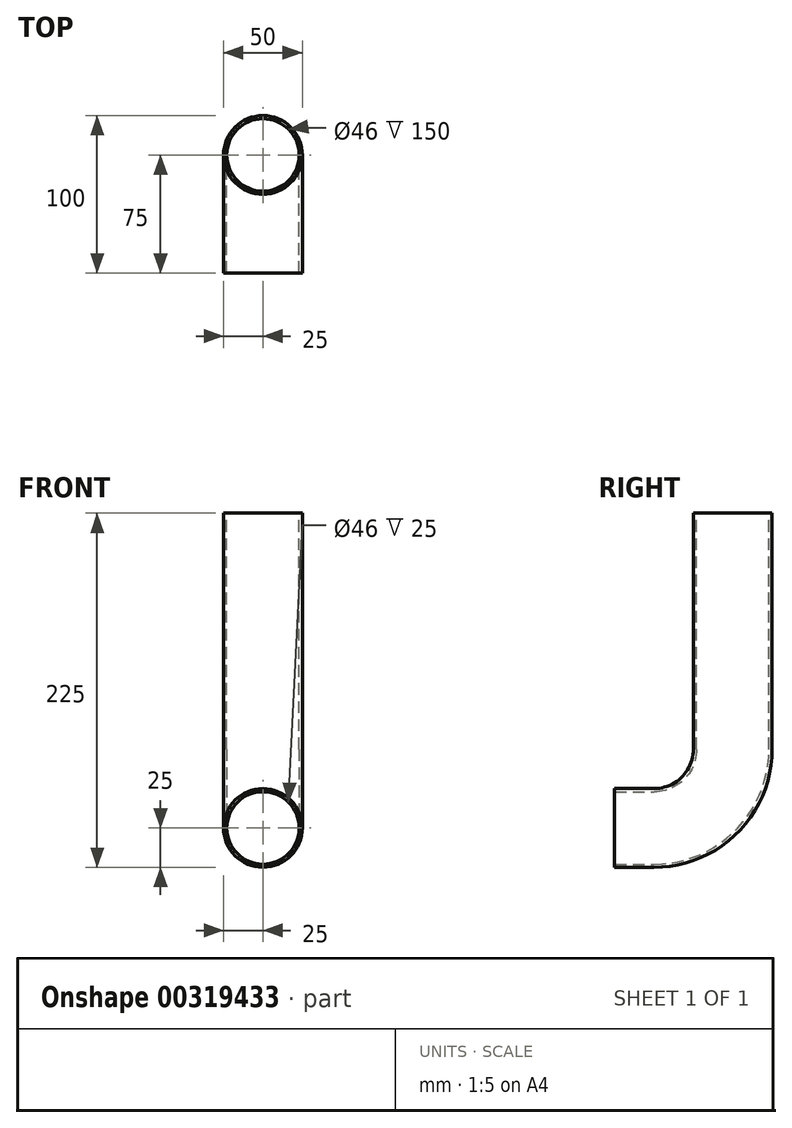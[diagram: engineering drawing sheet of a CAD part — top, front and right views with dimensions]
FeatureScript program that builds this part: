
annotation { "Feature Type Name" : "Feature", "Feature Type Description" : "" }
export const myFeature = defineFeature(function(context is Context, id is Id, definition is map)
    precondition{}
    {
        {
            var Q0;
            Q0=qCreatedBy(makeId("Front.planeOp"),FACE);
            var sketch = newSketch(context, id + "F0", { "sketchPlane" : qUnion([Q0])});
            skCircle(sketch, "E0", {"center": v(0, 0) * mm, "radius": 25 * mm});
            skCircle(sketch, "E1", {"center": v(0, 0) * mm, "radius": 23 * mm});
            skSolve(sketch);
        }
        {
            var Q0;
            Q0=qCreatedBy(makeId("Right.planeOp"),FACE);
            var sketch = newSketch(context, id + "F1", { "sketchPlane" : qUnion([Q0])});
            skLineSegment(sketch, "E2", {"start": v(0, 0) * mm, "end": v(25, 0) * mm});
            skLineSegment(sketch, "E3", {"start": v(75, 50) * mm, "end": v(75, 200) * mm});
            skArc(sketch, "E4", {"start": v(75, 50) * mm, "mid": v(60.36, 14.64) * mm, "end": v(25, 0) * mm});
            skSolve(sketch);
        }
        {
            var Q0;
            Q0 = qSketchRegion(id + "F0", true);
            var Q1;
            Q1 = qBodyType(qCreatedBy(id + "F1" ,EDGE), BodyType.WIRE);
            sweep(context, id + "F2", {"profiles" : qUnion([Q0]), "path" : qUnion([Q1])});
        }
    });
